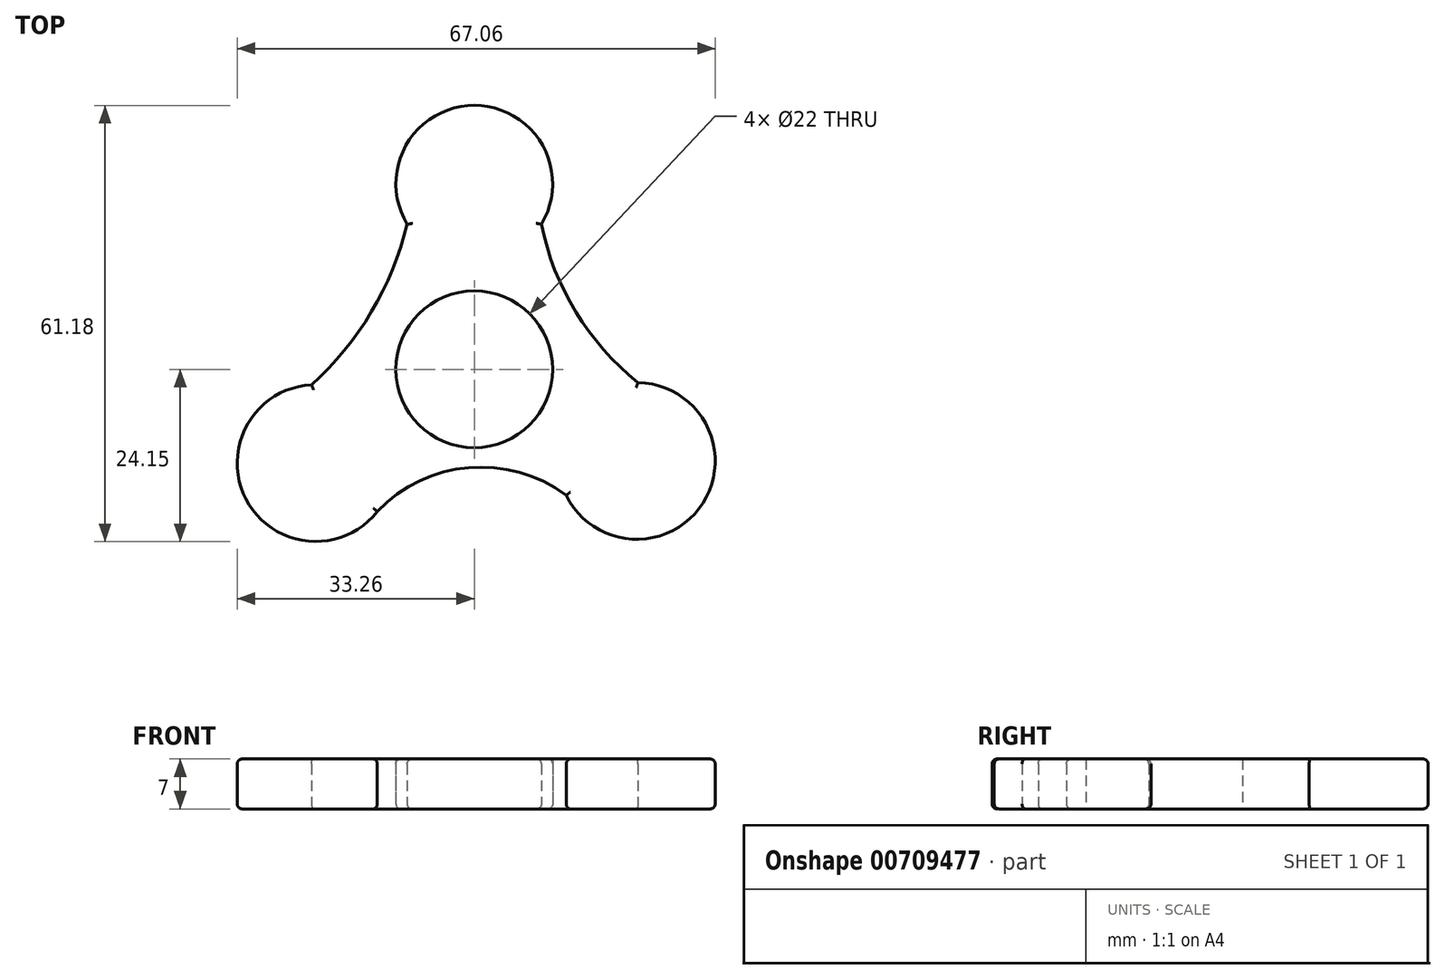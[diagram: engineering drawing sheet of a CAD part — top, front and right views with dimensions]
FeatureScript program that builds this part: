
annotation { "Feature Type Name" : "Feature", "Feature Type Description" : "" }
export const myFeature = defineFeature(function(context is Context, id is Id, definition is map)
    precondition{}
    {
        {
            var Q0;
            Q0=qCreatedBy(makeId("Top.planeOp"),FACE);
            var sketch = newSketch(context, id + "F0", { "sketchPlane" : qUnion([Q0])});
            skCircle(sketch, "E0", {"center": v(0, 0) * mm, "radius": 11 * mm});
            skArc(sketch, "E1", {"start": v(9.42, 20.35) * mm, "mid": v(0, 37.03) * mm, "end": v(-9.42, 20.35) * mm});
            skArc(sketch, "E2.1.0", {"start": v(-22.84, -2.16) * mm, "mid": v(-32.03, -18.21) * mm, "end": v(-13.62, -19.94) * mm});
            skArc(sketch, "E2.2.0", {"start": v(12.9, -17.66) * mm, "mid": v(32.08, -18.74) * mm, "end": v(22.97, -1.84) * mm});
            skPoint(sketch, "E2.center", {"position": v(0.18, 0.01) * mm});
            skArc(sketch, "E3", {"start": v(-22.84, -2.16) * mm, "mid": v(-14.43, 8.08) * mm, "end": v(-9.42, 20.35) * mm});
            skArc(sketch, "E4", {"start": v(12.9, -17.66) * mm, "mid": v(-0.78, -13.79) * mm, "end": v(-13.62, -19.94) * mm});
            skPoint(sketch, "E5.MirrorCS.start.orphan", {"position": v(22.84, -2.16) * mm});
            skArc(sketch, "E6", {"start": v(9.42, 20.35) * mm, "mid": v(14.23, 8.06) * mm, "end": v(22.97, -1.84) * mm});
            skSolve(sketch);
        }
        {
            var Q0;
            Q0=makeQuery(id+"F0.imprint","IMPRINT",FACE,{"disambiguationData":[TD([[makeQuery(id+"F0.imprint","IMPRINT",EDGE,{"derivedFrom":sQuery(id+"F0.wireOp",EDGE,"E0")}),-1.0]])]});
            extrude(context, id + "F1", {"entities" : qUnion([Q0]), "depth" : 7 * mm, "offsetDistance" : 25 * mm});
        }
        {
            var Q0;
            Q0=makeQuery(id+"F1.opExtrude","CAP_EDGE",EDGE,{"disambiguationData":[OSD([sQuery(id+"F0.wireOp",EDGE,"E1")])],"isStart":false});
            var Q1;
            Q1=makeQuery(id+"F1.opExtrude","CAP_EDGE",EDGE,{"disambiguationData":[OSD([sQuery(id+"F0.wireOp",EDGE,"E3")])],"isStart":false});
            var Q2;
            Q2=makeQuery(id+"F1.opExtrude","CAP_EDGE",EDGE,{"disambiguationData":[OSD([sQuery(id+"F0.wireOp",EDGE,"E2.1.0")])],"isStart":false});
            var Q3;
            Q3=makeQuery(id+"F1.opExtrude","CAP_EDGE",EDGE,{"disambiguationData":[OSD([sQuery(id+"F0.wireOp",EDGE,"E4")])],"isStart":false});
            var Q4;
            Q4=makeQuery(id+"F1.opExtrude","CAP_EDGE",EDGE,{"disambiguationData":[OSD([sQuery(id+"F0.wireOp",EDGE,"E6")])],"isStart":false});
            var Q5;
            Q5=makeQuery(id+"F1.opExtrude","CAP_EDGE",EDGE,{"disambiguationData":[OSD([sQuery(id+"F0.wireOp",EDGE,"E2.2.0")])],"isStart":false});
            fillet(context, id + "F2", {"entities" : qUnion([Q0, Q1, Q2, Q3, Q4, Q5]), "radius" : .7 * mm, "tangentPropagation" : true, "allowEdgeOverflow" : false});
        }
        {
            var Q0;
            Q0=makeQuery(id+"F1.opExtrude","CAP_EDGE",EDGE,{"disambiguationData":[OSD([sQuery(id+"F0.wireOp",EDGE,"E1")])],"isStart":true});
            var Q1;
            Q1=makeQuery(id+"F1.opExtrude","CAP_EDGE",EDGE,{"disambiguationData":[OSD([sQuery(id+"F0.wireOp",EDGE,"E6")])],"isStart":true});
            var Q2;
            Q2=makeQuery(id+"F1.opExtrude","CAP_EDGE",EDGE,{"disambiguationData":[OSD([sQuery(id+"F0.wireOp",EDGE,"E2.2.0")])],"isStart":true});
            var Q3;
            Q3=makeQuery(id+"F1.opExtrude","CAP_EDGE",EDGE,{"disambiguationData":[OSD([sQuery(id+"F0.wireOp",EDGE,"E4")])],"isStart":true});
            var Q4;
            Q4=makeQuery(id+"F1.opExtrude","CAP_EDGE",EDGE,{"disambiguationData":[OSD([sQuery(id+"F0.wireOp",EDGE,"E2.1.0")])],"isStart":true});
            var Q5;
            Q5=makeQuery(id+"F1.opExtrude","CAP_EDGE",EDGE,{"disambiguationData":[OSD([sQuery(id+"F0.wireOp",EDGE,"E3")])],"isStart":true});
            fillet(context, id + "F3", {"entities" : qUnion([Q0, Q1, Q2, Q3, Q4, Q5]), "radius" : .7 * mm, "tangentPropagation" : true, "allowEdgeOverflow" : false});
        }
    });
